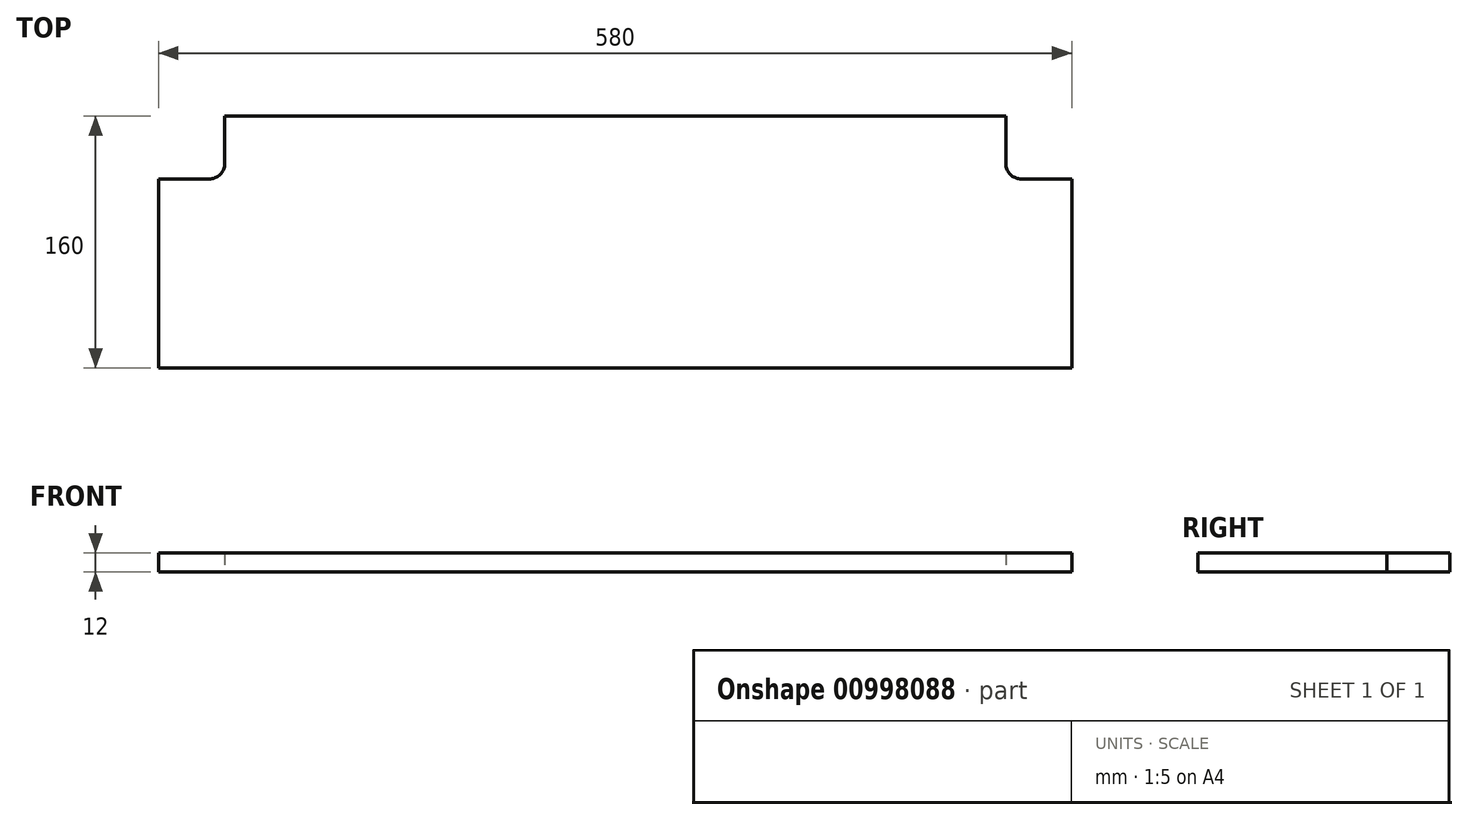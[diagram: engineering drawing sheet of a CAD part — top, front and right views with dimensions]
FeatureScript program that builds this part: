
annotation { "Feature Type Name" : "Feature", "Feature Type Description" : "" }
export const myFeature = defineFeature(function(context is Context, id is Id, definition is map)
    precondition{}
    {
        {
            var Q0;
            Q0=qCreatedBy(makeId("Top.planeOp"),FACE);
            var sketch = newSketch(context, id + "F0", { "sketchPlane" : qUnion([Q0])});
            skLineSegment(sketch, "E0", {"start": v(0, 0) * mm, "end": v(290, 0) * mm});
            skLineSegment(sketch, "E1", {"start": v(290, 0) * mm, "end": v(290, 120) * mm});
            skLineSegment(sketch, "E2", {"start": v(290, 120) * mm, "end": v(258, 120) * mm});
            skLineSegment(sketch, "E3", {"start": v(248, 130) * mm, "end": v(248, 160) * mm});
            skLineSegment(sketch, "E4", {"start": v(248, 160) * mm, "end": v(0, 160) * mm});
            skPoint(sketch, "E5.visualSharp", {"position": v(248, 120) * mm});
            skArc(sketch, "E5.filletArc", {"start": v(248, 130) * mm, "mid": v(250.93, 122.93) * mm, "end": v(258, 120) * mm});
            skArc(sketch, "E6.MirrorCS", {"start": v(-248, 130) * mm, "mid": v(-250.93, 122.93) * mm, "end": v(-258, 120) * mm});
            skLineSegment(sketch, "E7.MirrorCS", {"start": v(-290, 120) * mm, "end": v(-258, 120) * mm});
            skLineSegment(sketch, "E8.MirrorCS", {"start": v(-248, 130) * mm, "end": v(-248, 160) * mm});
            skPoint(sketch, "E9.MirrorP", {"position": v(-248, 120) * mm});
            skLineSegment(sketch, "E10.MirrorCS", {"start": v(-248, 160) * mm, "end": v(0, 160) * mm});
            skLineSegment(sketch, "E11.MirrorCS", {"start": v(-290, 0) * mm, "end": v(-290, 120) * mm});
            skLineSegment(sketch, "E12.MirrorCS", {"start": v(0, 0) * mm, "end": v(-290, 0) * mm});
            skSolve(sketch);
        }
        {
            var Q0;
            Q0 = qSketchRegion(id + "F0", true);
            extrude(context, id + "F1", {"entities" : qUnion([Q0]), "depth" : 12 * mm, "offsetDistance" : 25 * mm});
        }
    });
